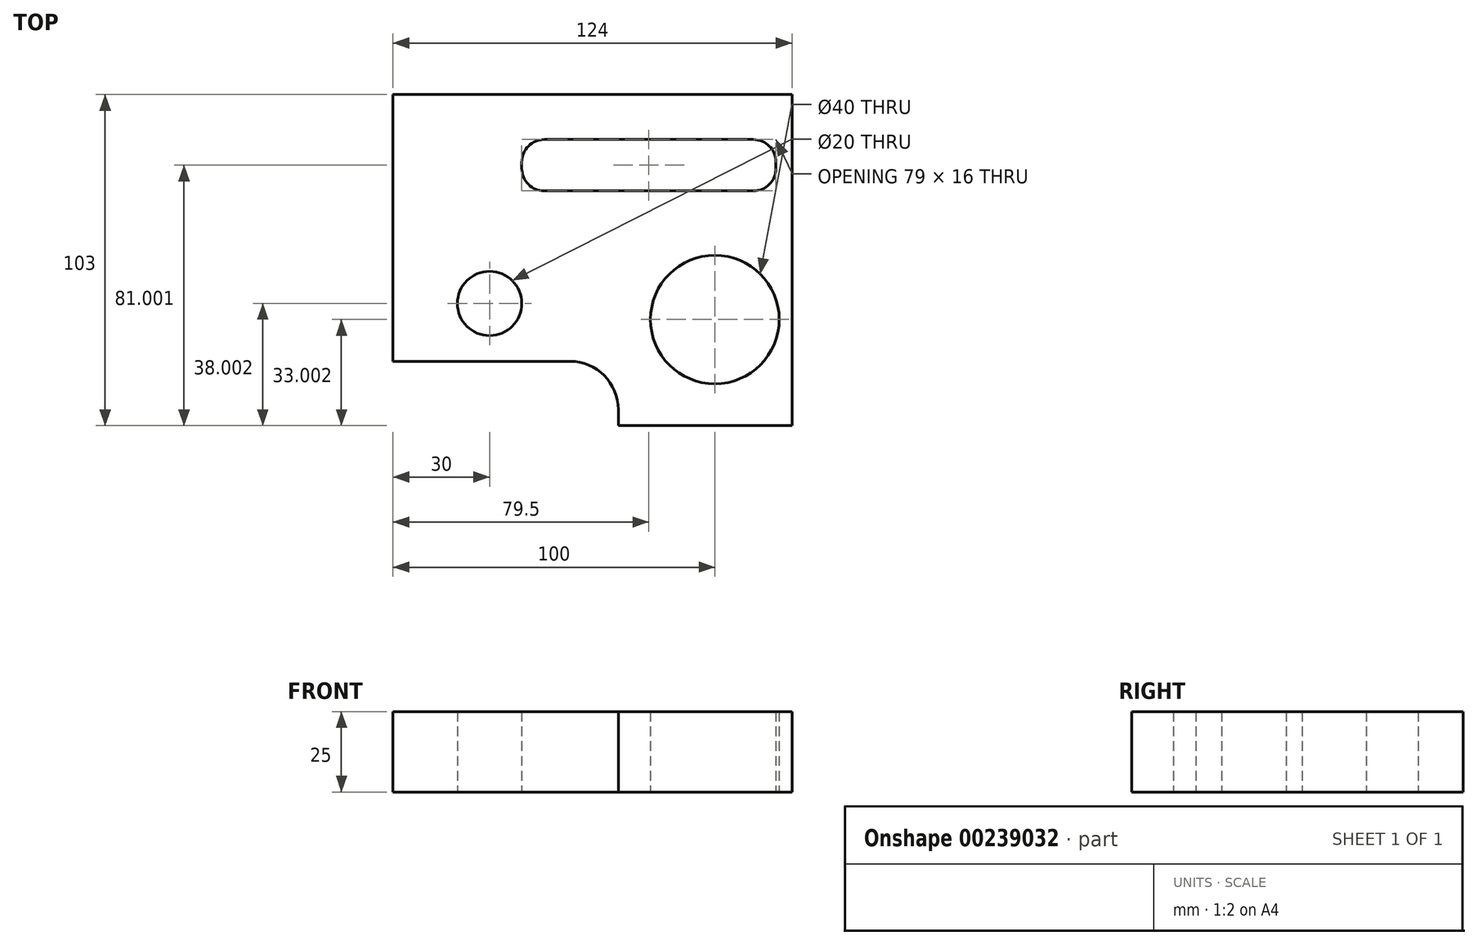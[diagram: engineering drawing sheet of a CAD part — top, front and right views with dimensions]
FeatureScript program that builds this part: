
annotation { "Feature Type Name" : "Feature", "Feature Type Description" : "" }
export const myFeature = defineFeature(function(context is Context, id is Id, definition is map)
    precondition{}
    {
        {
            var Q0;
            Q0=qCreatedBy(makeId("Top.planeOp"),FACE);
            var sketch = newSketch(context, id + "F0", { "sketchPlane" : qUnion([Q0])});
            skLineSegment(sketch, "E0", {"start": v(-54.68, 74.3) * mm, "end": v(69.32, 74.3) * mm});
            skLineSegment(sketch, "E1", {"start": v(69.32, 74.3) * mm, "end": v(69.32, -28.7) * mm});
            skLineSegment(sketch, "E2", {"start": v(69.32, -28.7) * mm, "end": v(15.32, -28.7) * mm});
            skLineSegment(sketch, "E3", {"start": v(15.32, -28.7) * mm, "end": v(15.32, -23.7) * mm});
            skLineSegment(sketch, "E4", {"start": v(-54.68, -8.7) * mm, "end": v(0.32, -8.7) * mm});
            skLineSegment(sketch, "E5", {"start": v(-54.68, 74.3) * mm, "end": v(-54.68, -8.7) * mm});
            skPoint(sketch, "E6.visualSharp", {"position": v(15.32, -8.7) * mm});
            skArc(sketch, "E6.filletArc", {"start": v(15.32, -23.7) * mm, "mid": v(10.93, -13.1) * mm, "end": v(0.32, -8.7) * mm});
            skCircle(sketch, "E7", {"center": v(45.32, 4.3) * mm, "radius": 20 * mm});
            skCircle(sketch, "E8", {"center": v(-24.68, 9.3) * mm, "radius": 10 * mm});
            skLineSegment(sketch, "E9.bottom", {"start": v(-7.68, 60.3) * mm, "end": v(57.32, 60.3) * mm});
            skLineSegment(sketch, "E9.top", {"start": v(-7.68, 44.3) * mm, "end": v(57.32, 44.3) * mm});
            skLineSegment(sketch, "E9.left", {"start": v(-14.68, 53.3) * mm, "end": v(-14.68, 51.3) * mm});
            skLineSegment(sketch, "E9.right", {"start": v(64.32, 53.3) * mm, "end": v(64.32, 51.3) * mm});
            skPoint(sketch, "E10.visualSharp", {"position": v(-14.68, 60.3) * mm});
            skArc(sketch, "E10.filletArc", {"start": v(-7.68, 60.3) * mm, "mid": v(-12.63, 58.24) * mm, "end": v(-14.68, 53.3) * mm});
            skPoint(sketch, "E11.visualSharp", {"position": v(-14.68, 44.3) * mm});
            skArc(sketch, "E11.filletArc", {"start": v(-14.68, 51.3) * mm, "mid": v(-12.63, 46.34) * mm, "end": v(-7.68, 44.3) * mm});
            skPoint(sketch, "E12.visualSharp", {"position": v(64.32, 60.3) * mm});
            skArc(sketch, "E12.filletArc", {"start": v(64.32, 53.3) * mm, "mid": v(62.27, 58.24) * mm, "end": v(57.32, 60.3) * mm});
            skPoint(sketch, "E13.visualSharp", {"position": v(64.32, 44.3) * mm});
            skArc(sketch, "E13.filletArc", {"start": v(57.32, 44.3) * mm, "mid": v(62.27, 46.34) * mm, "end": v(64.32, 51.3) * mm});
            skSolve(sketch);
        }
        {
            var Q0;
            Q0 = qSketchRegion(id + "F0", true);
            extrude(context, id + "F1", {"entities" : qUnion([Q0]), "depth" : 25 * mm});
        }
        {
            var Q0;
            Q0=makeQuery(id+"F0.imprint","IMPRINT",FACE,{"disambiguationData":[TD([[makeQuery(id+"F0.imprint","IMPRINT",EDGE,{"derivedFrom":sQuery(id+"F0.wireOp",EDGE,"E0")}),-1.0]])]});
            extrude(context, id + "F2", {"entities" : qUnion([Q0]), "operationType" : NewBodyOperationType.ADD, "depth" : 25 * mm});
        }
        {
            var Q0;
            Q0=makeQuery(id+"F0.imprint","IMPRINT",FACE,{"disambiguationData":[TD([[makeQuery(id+"F0.imprint","IMPRINT",EDGE,{"derivedFrom":sQuery(id+"F0.wireOp",EDGE,"E0")}),-1.0]])]});
            extrude(context, id + "F3", {"entities" : qUnion([Q0]), "operationType" : NewBodyOperationType.ADD, "depth" : 25 * mm});
        }
        {
            var Q0;
            Q0=makeQuery(id+"F0.imprint","IMPRINT",FACE,{"disambiguationData":[TD([[makeQuery(id+"F0.imprint","IMPRINT",EDGE,{"derivedFrom":sQuery(id+"F0.wireOp",EDGE,"E0")}),-1.0]])]});
            extrude(context, id + "F4", {"entities" : qUnion([Q0]), "operationType" : NewBodyOperationType.ADD, "depth" : 25 * mm});
        }
        {
            var Q0;
            Q0=makeQuery(id+"F0.imprint","IMPRINT",FACE,{"disambiguationData":[TD([[makeQuery(id+"F0.imprint","IMPRINT",EDGE,{"derivedFrom":sQuery(id+"F0.wireOp",EDGE,"E0")}),-1.0]])]});
            extrude(context, id + "F5", {"entities" : qUnion([Q0]), "operationType" : NewBodyOperationType.ADD, "depth" : 25 * mm});
        }
    });
